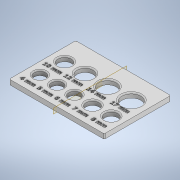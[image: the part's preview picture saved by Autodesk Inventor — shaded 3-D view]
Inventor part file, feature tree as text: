
AUTODESK INVENTOR PART (.ipt)
format: ipt  version: 2021 (Build 250183000, 183)  size: 1,061,888 bytes
history: native  units: in
note: dims shown in document units (in); Inventor stores cm internally (conversion verified against a paired STEP export)
features: extrude x3, sketch x3, fillet x2
ambient origin geometry x8: Origin, YZ Plane, XZ Plane, XY Plane, X Axis, Y Axis, Z Axis, Center Point
bodies: Solid1 (feature_tree)
feature tree (8):
  extrude  "Extrusion1"  Depth=3.5in
  extrude  "Extrusion3"  Depth=5.0in
  extrude  "Extrusion4"  Depth=0.0625in
  fillet  "Fillet1"  [1 undecoded]
  fillet  "Fillet2"  Radius=0.3454in
  sketch  "Sketch1"  dims[d0=0.25in d1=0.0in d3=3.5in]
  sketch  "Sketch4"  dims[d13=5.0in d16=1.0in]
  sketch  "Sketch7"  dims[d27=0.2883in d37=0.33in d38=0.0in d39=0.0in d45=0.3454in d46=1.6in d47=0.0938in d48=0.0in d49=0.0625in d50=0.0625in d51=0.5in d52=0.0344in d53=0.5in d54=0.0344in]
note: 1 required parameter value undecoded (feature->parameter linkage not recoverable at this tier; creation-order binding heuristic only, values carry confidence <= 0.55)
